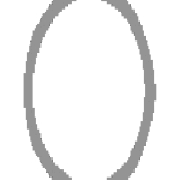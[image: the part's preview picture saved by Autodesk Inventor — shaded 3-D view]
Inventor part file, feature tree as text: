
AUTODESK INVENTOR PART (.ipt)
format: ipt  version: 2021 (Build 250183000, 183)  size: 109,056 bytes
history: native  units: in
note: dims shown in document units (in); Inventor stores cm internally (conversion verified against a paired STEP export)
features: other x4, sketch x3, plane x1
ambient origin geometry x8: Origin, YZ Plane, XZ Plane, XY Plane, X Axis, Y Axis, Z Axis, Center Point
bodies: Solid1 (feature_tree), Body (feature_tree)
feature tree (8):
  other  "Driven Length"
  other  "Frame Generator"
  other  "Start Plane"
  other  "End Plane"
  sketch  "Sketch"  dims[d2=38.7943in d4=-0.0in d5=38.7943in d6=0.12in d7=0.0in d8=90.0deg d9=38.7943in]
  sketch  "Sketch2"  dims[d0=1.0in]
  plane  "Work Plane3"
  sketch  "Sketch3"  dims[d1=0.065in]
